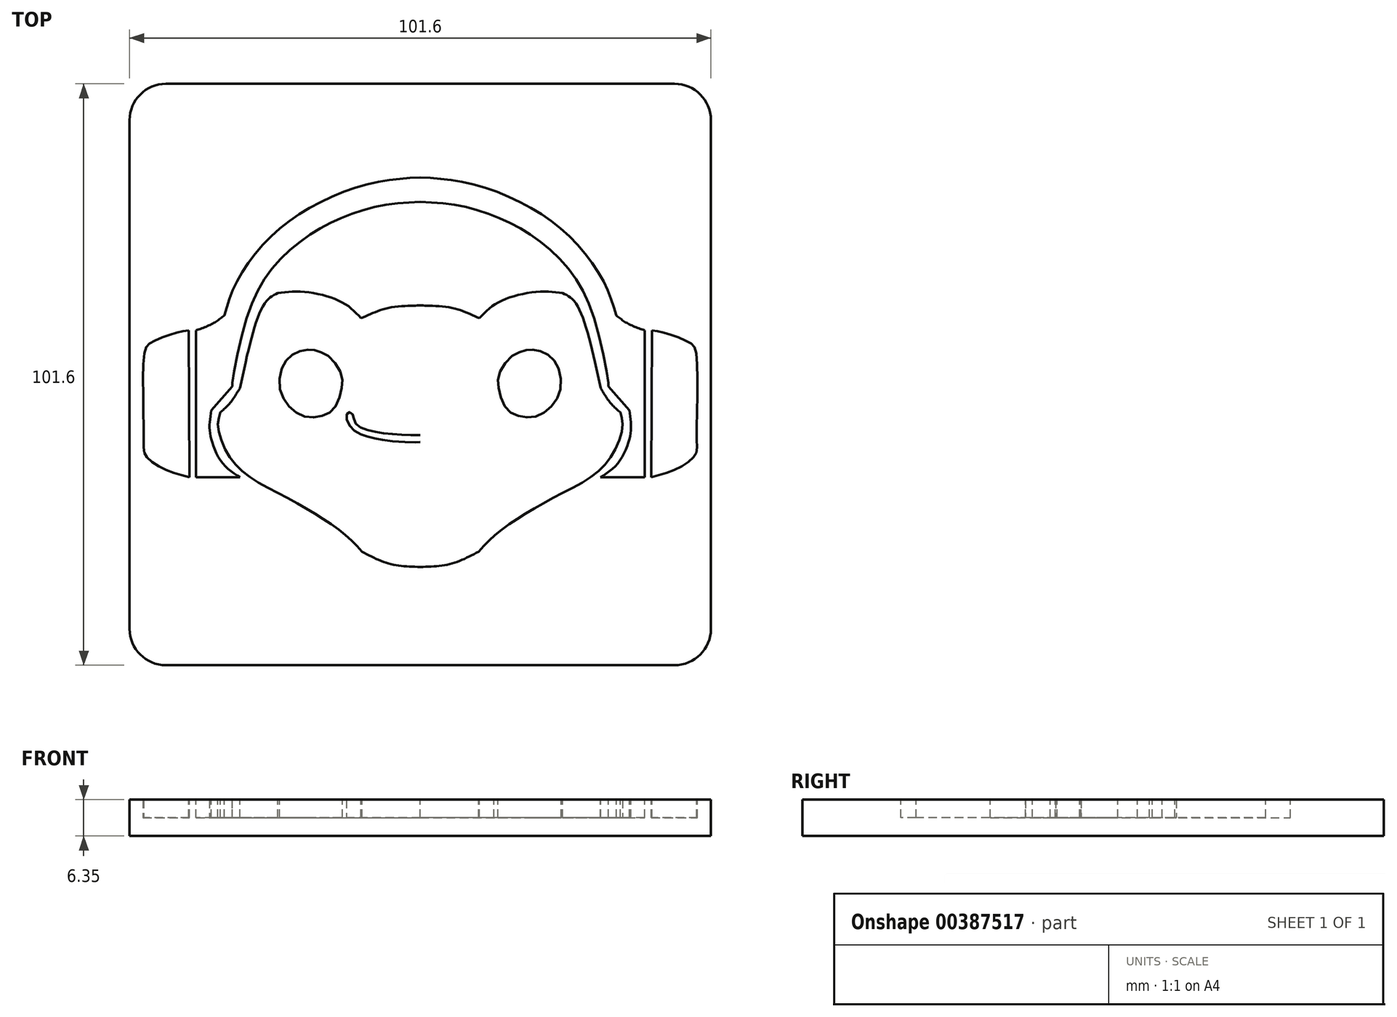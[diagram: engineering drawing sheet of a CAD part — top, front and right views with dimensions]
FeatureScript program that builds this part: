
annotation { "Feature Type Name" : "Feature", "Feature Type Description" : "" }
export const myFeature = defineFeature(function(context is Context, id is Id, definition is map)
    precondition{}
    {
        {
            var Q0;
            Q0=qCreatedBy(makeId("Top.planeOp"),FACE);
            var sketch = newSketch(context, id + "F0", { "sketchPlane" : qUnion([Q0])});
            skLineSegment(sketch, "E0.bottom", {"start": v(-44.45, 50.8) * mm, "end": v(44.45, 50.8) * mm});
            skLineSegment(sketch, "E0.top", {"start": v(-44.45, -50.8) * mm, "end": v(44.45, -50.8) * mm});
            skLineSegment(sketch, "E0.left", {"start": v(-50.8, 44.45) * mm, "end": v(-50.8, -44.45) * mm});
            skLineSegment(sketch, "E0.right", {"start": v(50.8, 44.45) * mm, "end": v(50.8, -44.45) * mm});
            skPoint(sketch, "E1.visualSharp", {"position": v(-50.8, 50.8) * mm});
            skArc(sketch, "E1.filletArc", {"start": v(-44.45, 50.8) * mm, "mid": v(-48.94, 48.94) * mm, "end": v(-50.8, 44.45) * mm});
            skPoint(sketch, "E2.visualSharp", {"position": v(50.8, 50.8) * mm});
            skArc(sketch, "E2.filletArc", {"start": v(50.8, 44.45) * mm, "mid": v(48.94, 48.94) * mm, "end": v(44.45, 50.8) * mm});
            skPoint(sketch, "E3.visualSharp", {"position": v(-50.8, -50.8) * mm});
            skArc(sketch, "E3.filletArc", {"start": v(-50.8, -44.45) * mm, "mid": v(-48.94, -48.94) * mm, "end": v(-44.45, -50.8) * mm});
            skPoint(sketch, "E4.visualSharp", {"position": v(50.8, -50.8) * mm});
            skArc(sketch, "E4.filletArc", {"start": v(44.45, -50.8) * mm, "mid": v(48.94, -48.94) * mm, "end": v(50.8, -44.45) * mm});
            skSolve(sketch);
        }
        {
            var Q0;
            Q0=qSketchRegion(id+"F0",true);
            extrude(context, id + "F1", {"entities" : qUnion([Q0]), "depth" : 6.35 * mm});
        }
        {
            var Q0;
            Q0=makeQuery(id+"F1.opExtrude","CAP_FACE",FACE,{"disambiguationData":[OSD([sQuery(id+"F0.wireOp",EDGE,"E0.bottom"),sQuery(id+"F0.wireOp",EDGE,"E0.top"),sQuery(id+"F0.wireOp",EDGE,"E0.left"),sQuery(id+"F0.wireOp",EDGE,"E0.right"),sQuery(id+"F0.wireOp",EDGE,"E1.filletArc"),sQuery(id+"F0.wireOp",EDGE,"E2.filletArc"),sQuery(id+"F0.wireOp",EDGE,"E3.filletArc"),sQuery(id+"F0.wireOp",EDGE,"E4.filletArc")])],"isStart":false});
            var sketch = newSketch(context, id + "F2", { "sketchPlane" : qUnion([Q0])});
            skFitSpline(sketch, "E5", {"points": [v(-24.89, 14.25) * mm, v(-27.23, 12.37) * mm, v(-31.52, -2.38) * mm], "startDerivative": vector(-7.87, -3.8) * mm, "endDerivative": vector(-5.68, -26.52) * mm});
            skFitSpline(sketch, "E6", {"points": [v(-31.52, -2.38) * mm, v(-33.26, -5) * mm, v(-34.94, -6.6) * mm], "startDerivative": vector(-3.14, -5.23) * mm, "endDerivative": vector(-3.71, -3.16) * mm});
            skFitSpline(sketch, "E7", {"points": [v(-34.94, -6.6) * mm, v(-35.36, -9) * mm, v(-33.65, -13.85) * mm, v(-29.88, -17.88) * mm, v(-23.23, -21.57) * mm, v(-17.3, -25.03) * mm, v(-12.94, -28.16) * mm, v(-10.2, -30.95) * mm], "startDerivative": vector(-7.2, -21.92) * mm, "endDerivative": vector(20.36, -22.6) * mm});
            skFitSpline(sketch, "E8", {"points": [v(-10.2, -30.95) * mm, v(-5.4, -33.06) * mm, v(0, -33.63) * mm], "startDerivative": vector(9.4, -5.03) * mm, "endDerivative": vector(10.97, -0.34) * mm});
            skFitSpline(sketch, "E9", {"points": [v(-24.89, 14.25) * mm, v(-21.4, 14.5) * mm, v(-16.37, 13.7) * mm, v(-12.62, 11.97) * mm, v(-10.36, 9.83) * mm], "startDerivative": vector(13.95, 1.85) * mm, "endDerivative": vector(9.25, -10.17) * mm});
            skFitSpline(sketch, "E10", {"points": [v(-10.36, 9.83) * mm, v(-8, 10.86) * mm, v(-4.88, 11.76) * mm, v(-1.13, 12.04) * mm, v(0, 12.06) * mm], "startDerivative": vector(9.19, 4.21) * mm, "endDerivative": vector(5.68, 0.03) * mm});
            skFitSpline(sketch, "E11", {"points": [v(-19.65, 4.33) * mm, v(-22.07, 3.64) * mm, v(-23.97, 1.58) * mm, v(-24.54, -2.38) * mm, v(-22.9, -5.56) * mm, v(-20.13, -7.33) * mm, v(-17.2, -7.26) * mm, v(-14.99, -5.87) * mm, v(-13.75, -2.55) * mm, v(-13.78, 0) * mm, v(-15.84, 3.05) * mm, v(-18.04, 4.14) * mm, v(-19.65, 4.33) * mm]});
            skFitSpline(sketch, "E12", {"points": [v(0, -10.6) * mm, v(-5.07, -10.4) * mm, v(-9.16, -9.73) * mm, v(-11.3, -8.53) * mm, v(-11.74, -7.1) * mm, v(-12.43, -6.56) * mm, v(-12.9, -7.3) * mm, v(-11.85, -9.5) * mm, v(-9.16, -10.87) * mm, v(-5.1, -11.61) * mm, v(0, -11.8) * mm, v(0, -11.77) * mm], "startDerivative": vector(-38.3, 0.78) * mm, "endDerivative": vector(-1.42, 2.68) * mm});
            skFitSpline(sketch, "E13", {"points": [v(0, 30.15) * mm, v(-6.76, 29.52) * mm, v(-13.7, 27.37) * mm, v(-19.95, 23.97) * mm, v(-26.25, 18.03) * mm, v(-30.84, 8.17) * mm, v(-32.9, -2.1) * mm, v(-32.86, -2.1) * mm], "startDerivative": vector(-45.5, -2.07) * mm, "endDerivative": vector(3.29, 1.57) * mm});
            skFitSpline(sketch, "E14", {"points": [v(-32.86, -2.1) * mm, v(-36.53, -6.27) * mm], "startDerivative": vector(-3.67, -4.17) * mm, "endDerivative": vector(-3.67, -4.17) * mm});
            skFitSpline(sketch, "E15", {"points": [v(-36.53, -6.27) * mm, v(-36.82, -8.85) * mm, v(-36.53, -11.28) * mm, v(-34.68, -15.33) * mm, v(-31.5, -17.97) * mm], "startDerivative": vector(-1.76, -12.05) * mm, "endDerivative": vector(12.4, -8.07) * mm});
            skFitSpline(sketch, "E16", {"points": [v(-31.5, -17.97) * mm, v(-39.2, -17.97) * mm], "startDerivative": vector(-7.7, 0) * mm, "endDerivative": vector(-7.7, 0) * mm});
            skFitSpline(sketch, "E17", {"points": [v(-39.2, -17.97) * mm, v(-39.2, 7.71) * mm], "startDerivative": vector(0, 25.68) * mm, "endDerivative": vector(0, 25.68) * mm});
            skFitSpline(sketch, "E18", {"points": [v(-39.2, 7.71) * mm, v(-36.25, 8.92) * mm, v(-34.25, 10.33) * mm], "startDerivative": vector(5.86, 2.07) * mm, "endDerivative": vector(4, 3.2) * mm});
            skFitSpline(sketch, "E19", {"points": [v(-34.25, 10.33) * mm, v(-32.22, 15.9) * mm, v(-26.86, 23.35) * mm, v(-18.57, 29.56) * mm, v(-8.1, 33.54) * mm, v(0, 34.44) * mm], "startDerivative": vector(9.67, 33.1) * mm, "endDerivative": vector(40.71, 2.06) * mm});
            skFitSpline(sketch, "E20", {"points": [v(-40.47, 7.71) * mm, v(-40.36, -17.97) * mm], "startDerivative": vector(0.11, -25.68) * mm, "endDerivative": vector(0.11, -25.68) * mm});
            skFitSpline(sketch, "E21", {"points": [v(-40.36, -17.97) * mm, v(-44.84, -16.46) * mm, v(-48.01, -14.14) * mm, v(-48.33, -11.36) * mm, v(-48.25, 3.65) * mm, v(-47.12, 5.54) * mm, v(-43.26, 7.12) * mm, v(-40.47, 7.71) * mm], "startDerivative": vector(-30.96, 8.3) * mm, "endDerivative": vector(22.64, 3.58) * mm});
            skFitSpline(sketch, "E22.MirrorCS", {"points": [v(34.25, 10.33) * mm, v(32.22, 15.9) * mm, v(26.86, 23.35) * mm, v(18.57, 29.56) * mm, v(8.1, 33.54) * mm, v(0, 34.44) * mm], "startDerivative": vector(-9.67, 33.1) * mm, "endDerivative": vector(-40.71, 2.06) * mm});
            skFitSpline(sketch, "E23.MirrorCS", {"points": [v(0, 30.15) * mm, v(6.76, 29.52) * mm, v(13.7, 27.37) * mm, v(19.95, 23.97) * mm, v(26.25, 18.03) * mm, v(30.84, 8.17) * mm, v(32.9, -2.1) * mm, v(32.86, -2.1) * mm], "startDerivative": vector(45.5, -2.07) * mm, "endDerivative": vector(-3.29, 1.57) * mm});
            skFitSpline(sketch, "E24.MirrorCS", {"points": [v(10.36, 9.83) * mm, v(8, 10.86) * mm, v(4.88, 11.76) * mm, v(1.13, 12.04) * mm, v(0, 12.06) * mm], "startDerivative": vector(-9.19, 4.21) * mm, "endDerivative": vector(-5.68, 0.03) * mm});
            skFitSpline(sketch, "E25.MirrorCS", {"points": [v(24.89, 14.25) * mm, v(21.4, 14.5) * mm, v(16.37, 13.7) * mm, v(12.62, 11.97) * mm, v(10.36, 9.83) * mm], "startDerivative": vector(-13.95, 1.85) * mm, "endDerivative": vector(-9.25, -10.17) * mm});
            skFitSpline(sketch, "E26.MirrorCS", {"points": [v(24.89, 14.25) * mm, v(27.23, 12.37) * mm, v(31.52, -2.38) * mm], "startDerivative": vector(7.87, -3.8) * mm, "endDerivative": vector(5.68, -26.52) * mm});
            skFitSpline(sketch, "E27.MirrorCS", {"points": [v(31.52, -2.38) * mm, v(33.26, -5) * mm, v(34.94, -6.6) * mm], "startDerivative": vector(3.14, -5.23) * mm, "endDerivative": vector(3.71, -3.16) * mm});
            skFitSpline(sketch, "E28.MirrorCS", {"points": [v(34.94, -6.6) * mm, v(35.36, -9) * mm, v(33.65, -13.85) * mm, v(29.88, -17.88) * mm, v(23.23, -21.57) * mm, v(17.3, -25.03) * mm, v(12.94, -28.16) * mm, v(10.2, -30.95) * mm], "startDerivative": vector(7.2, -21.92) * mm, "endDerivative": vector(-20.36, -22.6) * mm});
            skFitSpline(sketch, "E29.MirrorCS", {"points": [v(10.2, -30.95) * mm, v(5.4, -33.06) * mm, v(0, -33.63) * mm], "startDerivative": vector(-9.4, -5.03) * mm, "endDerivative": vector(-10.97, -0.34) * mm});
            skFitSpline(sketch, "E30.MirrorCS", {"points": [v(0, -10.6) * mm, v(5.07, -10.4) * mm, v(9.16, -9.73) * mm, v(11.3, -8.53) * mm, v(11.74, -7.1) * mm, v(12.43, -6.56) * mm, v(12.9, -7.3) * mm, v(11.85, -9.5) * mm, v(9.16, -10.87) * mm, v(5.1, -11.61) * mm, v(0, -11.8) * mm, v(0, -11.77) * mm], "startDerivative": vector(38.3, 0.78) * mm, "endDerivative": vector(1.42, 2.68) * mm});
            skFitSpline(sketch, "E31.MirrorC", {"points": [v(19.65, 4.33) * mm, v(22.07, 3.64) * mm, v(23.97, 1.58) * mm, v(24.54, -2.38) * mm, v(22.9, -5.56) * mm, v(20.13, -7.33) * mm, v(17.2, -7.26) * mm, v(14.99, -5.87) * mm, v(13.75, -2.55) * mm, v(13.78, 0) * mm, v(15.84, 3.05) * mm, v(18.04, 4.14) * mm, v(19.65, 4.33) * mm]});
            skFitSpline(sketch, "E32.MirrorCS", {"points": [v(39.2, -17.97) * mm, v(39.2, 7.71) * mm], "startDerivative": vector(0, 25.68) * mm, "endDerivative": vector(0, 25.68) * mm});
            skFitSpline(sketch, "E33.MirrorCS", {"points": [v(39.2, 7.71) * mm, v(36.25, 8.92) * mm, v(34.25, 10.33) * mm], "startDerivative": vector(-5.86, 2.07) * mm, "endDerivative": vector(-4, 3.2) * mm});
            skFitSpline(sketch, "E34.MirrorCS", {"points": [v(32.86, -2.1) * mm, v(36.53, -6.27) * mm], "startDerivative": vector(3.67, -4.17) * mm, "endDerivative": vector(3.67, -4.17) * mm});
            skFitSpline(sketch, "E35.MirrorCS", {"points": [v(36.53, -6.27) * mm, v(36.82, -8.85) * mm, v(36.53, -11.28) * mm, v(34.68, -15.33) * mm, v(31.5, -17.97) * mm], "startDerivative": vector(1.76, -12.05) * mm, "endDerivative": vector(-12.4, -8.07) * mm});
            skFitSpline(sketch, "E36.MirrorCS", {"points": [v(31.5, -17.97) * mm, v(39.2, -17.97) * mm], "startDerivative": vector(7.7, 0) * mm, "endDerivative": vector(7.7, 0) * mm});
            skFitSpline(sketch, "E37.MirrorCS", {"points": [v(40.47, 7.71) * mm, v(40.36, -17.97) * mm], "startDerivative": vector(-0.11, -25.68) * mm, "endDerivative": vector(-0.11, -25.68) * mm});
            skFitSpline(sketch, "E38.MirrorCS", {"points": [v(40.36, -17.97) * mm, v(44.84, -16.46) * mm, v(48.01, -14.14) * mm, v(48.33, -11.36) * mm, v(48.25, 3.65) * mm, v(47.12, 5.54) * mm, v(43.26, 7.12) * mm, v(40.47, 7.71) * mm], "startDerivative": vector(30.96, 8.3) * mm, "endDerivative": vector(-22.64, 3.58) * mm});
            skSolve(sketch);
        }
        {
            var Q0;
            Q0=qSketchRegion(id+"F2",true);
            extrude(context, id + "F3", {"entities" : qUnion([Q0]), "operationType" : NewBodyOperationType.REMOVE, "oppositeDirection" : true, "depth" : 3.17 * mm});
        }
    });
